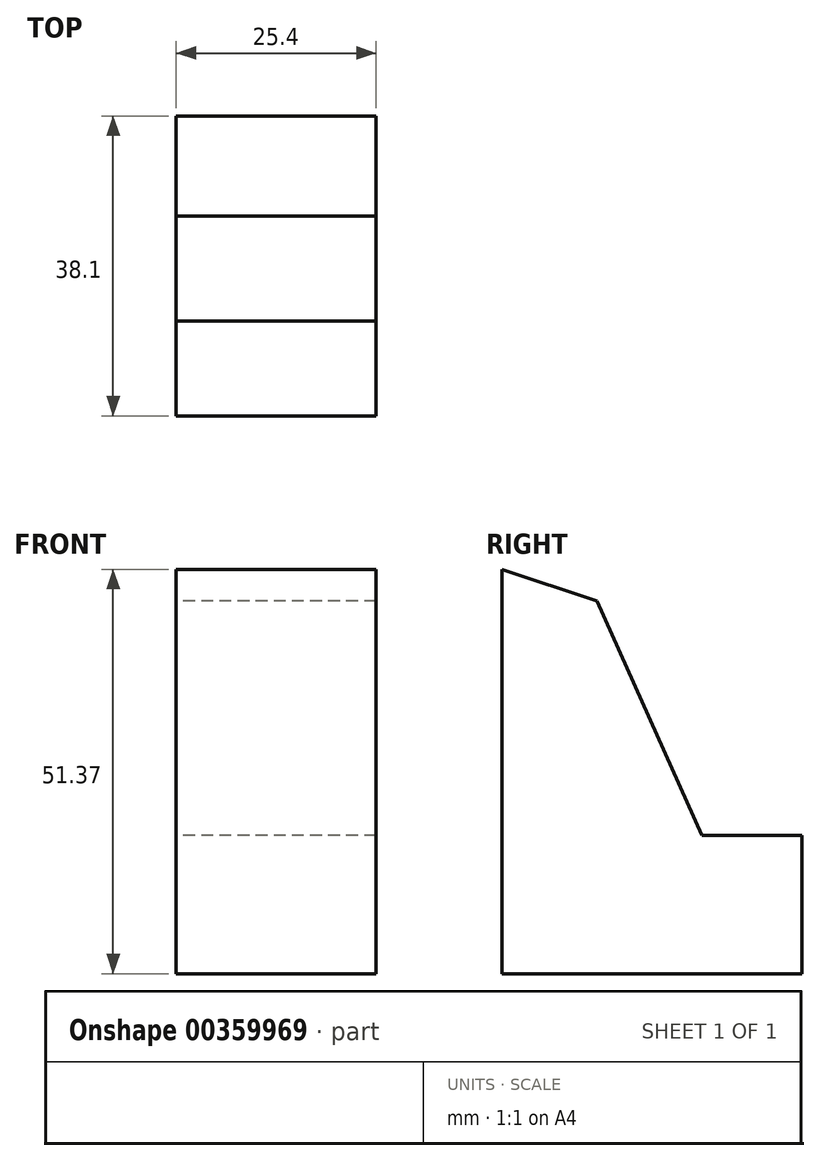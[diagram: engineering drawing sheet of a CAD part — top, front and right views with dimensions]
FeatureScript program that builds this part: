
annotation { "Feature Type Name" : "Feature", "Feature Type Description" : "" }
export const myFeature = defineFeature(function(context is Context, id is Id, definition is map)
    precondition{}
    {
        {
            var Q0;
            Q0=qCreatedBy(makeId("Right.planeOp"),FACE);
            var sketch = newSketch(context, id + "F0", { "sketchPlane" : qUnion([Q0])});
            skLineSegment(sketch, "E0", {"start": v(0, 51.37) * mm, "end": v(12.05, 47.36) * mm});
            skLineSegment(sketch, "E1", {"start": v(12.05, 47.36) * mm, "end": v(25.4, 17.57) * mm});
            skLineSegment(sketch, "E2", {"start": v(25.4, 17.57) * mm, "end": v(38.1, 17.57) * mm});
            skLineSegment(sketch, "E3", {"start": v(38.1, 17.57) * mm, "end": v(38.1, 0) * mm});
            skLineSegment(sketch, "E4", {"start": v(38.1, 0) * mm, "end": v(0, 0) * mm});
            skLineSegment(sketch, "E5", {"start": v(0, 0) * mm, "end": v(0, 51.37) * mm});
            skSolve(sketch);
        }
        {
            var Q0;
            Q0 = qSketchRegion(id + "F0", true);
            extrude(context, id + "F1", {"entities" : qUnion([Q0]), "depth" : 25.4 * mm});
        }
    });
